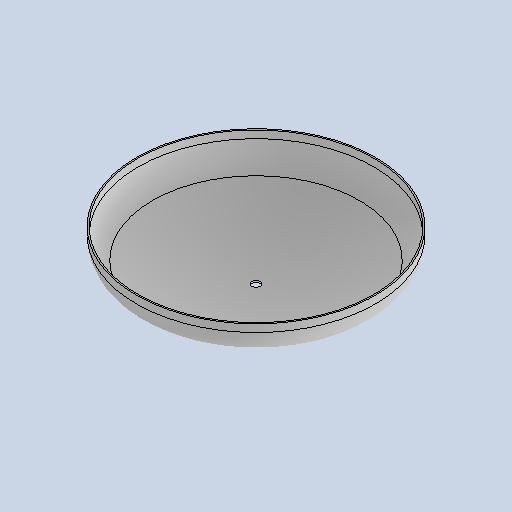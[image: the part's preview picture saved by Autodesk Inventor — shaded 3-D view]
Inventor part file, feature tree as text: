
AUTODESK INVENTOR PART (.ipt)
format: ipt  version: 2025.1 (Build 291241020, 241B)  size: 164,352 bytes
history: native  units: mm
features: sketch x2, revolve x1, extrude x1
ambient origin geometry x8: Origin, YZ Plane, XZ Plane, XY Plane, X Axis, Y Axis, Z Axis, Center Point
bodies: Solid1 (feature_tree)
feature tree (4):
  revolve  "Revolution1"  [1 undecoded]
  extrude  "Extrusion1"  Depth=1080.006667mm
  sketch  "Sketch1"  dims[d0=100.0mm d1=30.0mm]
  sketch  "Sketch2"  dims[d3=1080.006667mm d6=6.0mm d7=90.0deg d8=33.5mm d9=0.0mm d10=0.0mm d11=940.0mm d12=205.0mm]
note: 1 required parameter value undecoded (feature->parameter linkage not recoverable at this tier; creation-order binding heuristic only, values carry confidence <= 0.55)
